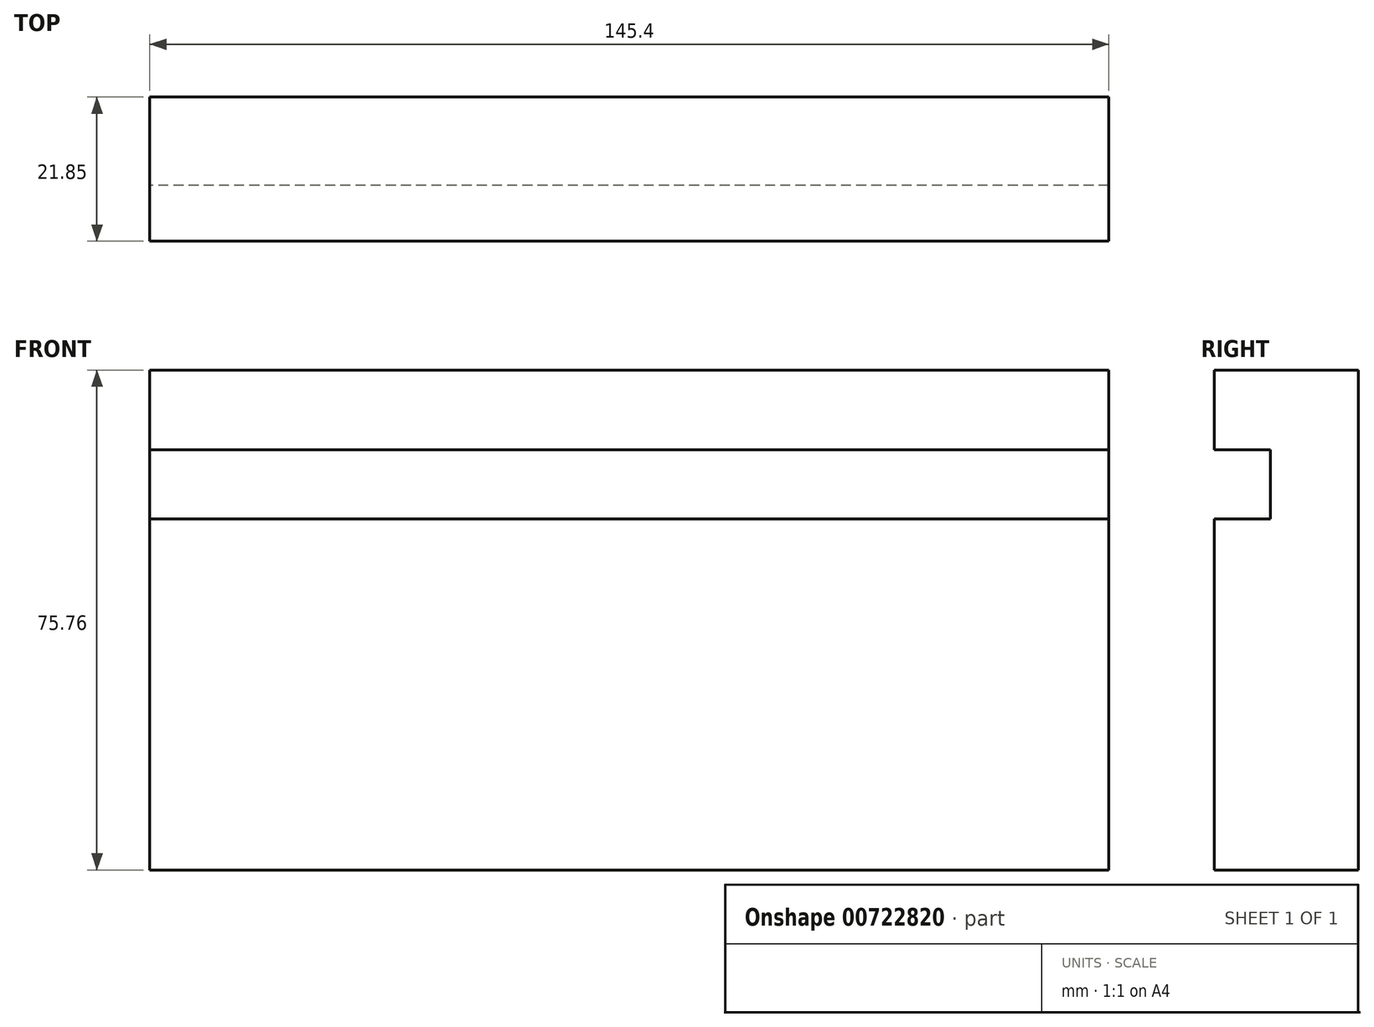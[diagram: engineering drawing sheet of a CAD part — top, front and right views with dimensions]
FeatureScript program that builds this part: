
annotation { "Feature Type Name" : "Feature", "Feature Type Description" : "" }
export const myFeature = defineFeature(function(context is Context, id is Id, definition is map)
    precondition{}
    {
        {
            var Q0;
            Q0=qCreatedBy(makeId("Right.planeOp"),FACE);
            var sketch = newSketch(context, id + "F0", { "sketchPlane" : qUnion([Q0])});
            skLineSegment(sketch, "E0", {"start": v(0, 0) * mm, "end": v(0, 75.76) * mm});
            skLineSegment(sketch, "E1", {"start": v(0, 75.76) * mm, "end": v(-21.85, 75.76) * mm});
            skLineSegment(sketch, "E2", {"start": v(-21.85, 63.7) * mm, "end": v(-13.37, 63.7) * mm});
            skLineSegment(sketch, "E3", {"start": v(-13.37, 63.7) * mm, "end": v(-13.37, 53.19) * mm});
            skLineSegment(sketch, "E4", {"start": v(-13.37, 53.19) * mm, "end": v(-21.85, 53.19) * mm});
            skLineSegment(sketch, "E5", {"start": v(-21.85, 53.19) * mm, "end": v(-21.85, 0) * mm});
            skLineSegment(sketch, "E6", {"start": v(-21.85, 0) * mm, "end": v(0, 0) * mm});
            skLineSegment(sketch, "E7", {"start": v(-21.85, 63.7) * mm, "end": v(-21.85, 75.76) * mm});
            skSolve(sketch);
        }
        {
            var Q0;
            Q0=qSketchRegion(id+"F0",true);
            extrude(context, id + "F1", {"entities" : qUnion([Q0]), "depth" : 120 * mm, "offsetDistance" : 25.4 * mm, "hasSecondDirection" : true, "secondDirectionOppositeDirection" : true, "secondDirectionDepth" : 25.4 * mm});
        }
    });
